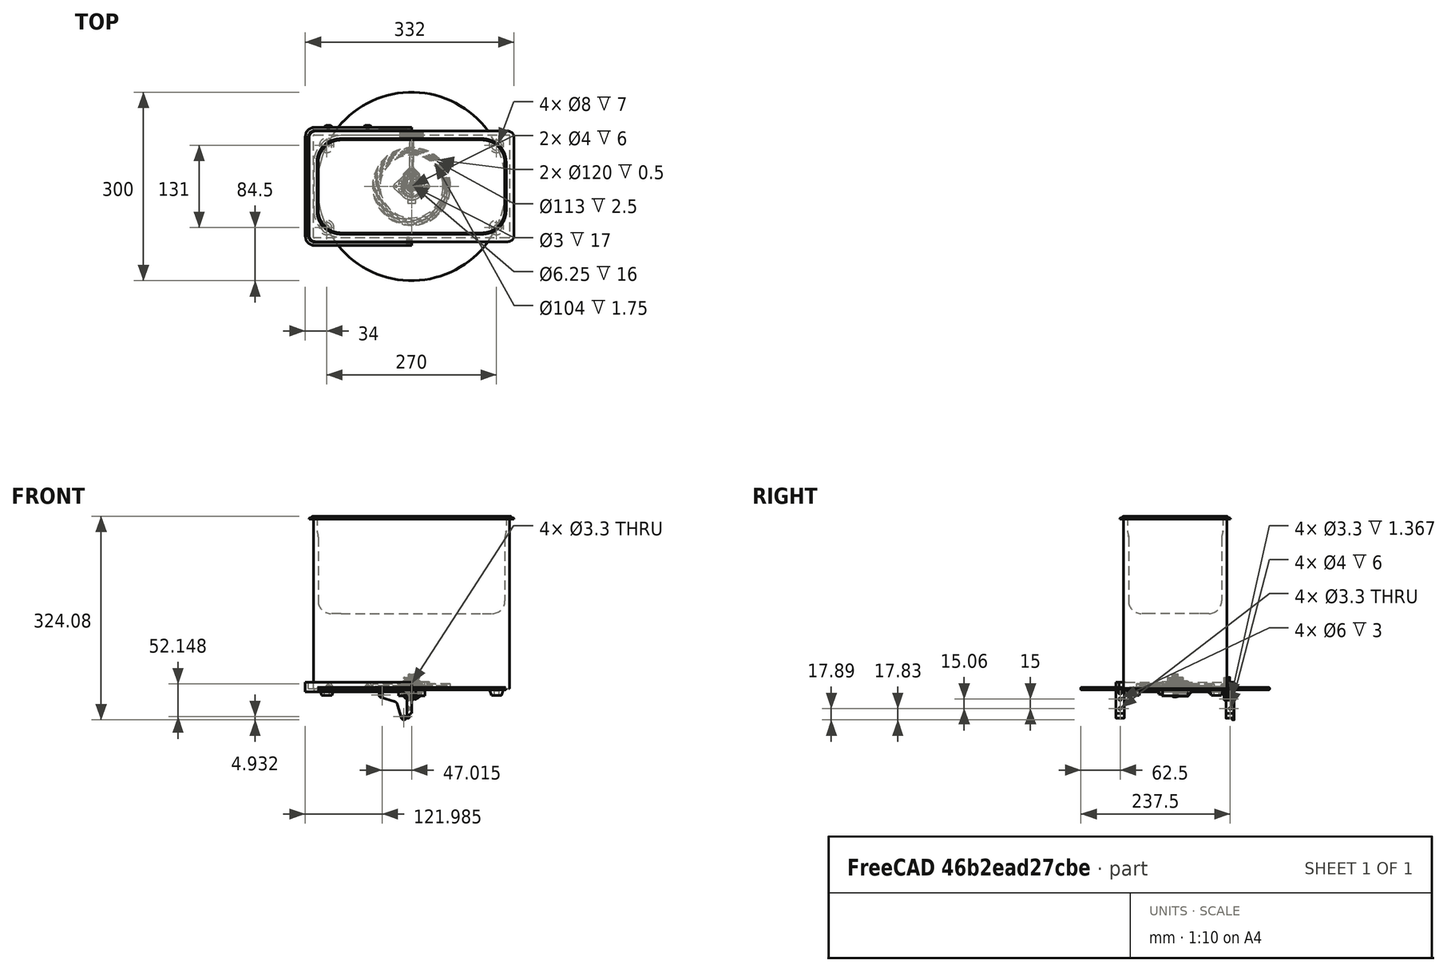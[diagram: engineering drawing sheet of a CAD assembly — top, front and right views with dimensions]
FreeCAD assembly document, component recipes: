
FREECAD ASSEMBLY — COMPONENT RECIPES ("assembly-ultrasonic-cleaner-exploded")

This assembly document has 14 components, labeled P0..P13 below (a component is one placed body or linked part). 14 of them carry a construction recipe — the FreeCAD feature program that regenerates the part from scratch, quoted from this document or its linked companion documents; the rest are supplied as boundary geometry only. No exploded tour is included for this assembly.
NOTE — document 2 of 2 of this assembly tour. The two overview renders and the header above are repeated from document 1; the component sections below continue where the previous document stopped.
COMPONENT P11 — recipe-attached ("Body011", modeled in this document).
Construction recipe (the document's own serialized feature program — sketch geometry with constraints, then the solid features built on it; lengths are millimeters unless a unit is written):

FEATURE [Sketcher::SketchObject] Sketch055
  ArcFitTolerance = 0
  AttachmentSupport = -> [XY_Plane011]
  ExternalBSplineMaxDegree = 0
  ExternalBSplineTolerance = 0
  FullyConstrained = false
  InternalTolerance = 1e-06
  InvalidShape = false
  MakeInternals = false
  MapMode = 5
  Support = -> [XY_Plane011]
  TreeRank = 0
  ValidateShape = false
  sketch-geometry (1):
    g0: Circle CenterX=0 CenterY=0 CenterZ=0 NormalX=0 NormalY=0 NormalZ=1 AngleXU=0 Radius=15
  constraints (2):
    c: Coincident(g0,g-1)
    c: Diameter(g0) = 30
FEATURE [PartDesign::Pad] Pad027
  AddSubType = 0
  AutoTaperInnerAngle = true
  CheckUpToFaceLimits = true
  ClaimChildren = false
  Direction = (1,1,1)
  Fit = 0
  FitJoin = 0
  InnerFit = 0
  InnerFitJoin = 0
  InvalidShape = false
  Length = 9
  Length2 = 100
  NewSolid = false
  Profile = -> Sketch055
  Suppress = false
  TaperInnerAngle = 0
  TaperInnerAngleRev = 0
  TreeRank = 0
  Type = 0
  ValidateShape = true
  _ProfileBasedVersion = 0
FEATURE [Sketcher::SketchObject] Sketch056
  ArcFitTolerance = 0
  AttachmentSupport = -> [Pad027]
  ExternalBSplineMaxDegree = 0
  ExternalBSplineTolerance = 0
  FullyConstrained = false
  InternalTolerance = 1e-06
  InvalidShape = false
  MakeInternals = false
  MapMode = 5
  Placement = pos=(0,0,9) rot=(0,0,1;0rad)
  Support = -> [Pad027]
  TreeRank = 0
  ValidateShape = false
  sketch-geometry (1):
    g0: Circle CenterX=0 CenterY=0 CenterZ=0 NormalX=0 NormalY=0 NormalZ=1 AngleXU=0 Radius=2
  constraints (2):
    c: Coincident(g0,g-1)
    c: Diameter(g0) = 4
FEATURE [PartDesign::Pocket] Pocket028
  AddSubType = 1
  AutoTaperInnerAngle = true
  BaseFeature = -> Pad027
  CheckUpToFaceLimits = true
  ClaimChildren = false
  Direction = (1,1,1)
  Fit = 0
  FitJoin = 0
  InnerFit = 0
  InnerFitJoin = 0
  InvalidShape = false
  Length = 8
  Length2 = 100
  NewSolid = false
  Profile = -> Sketch056
  Suppress = false
  TaperInnerAngle = 0
  TaperInnerAngleRev = 0
  TreeRank = 0
  Type = 0
  ValidateShape = true
  _ProfileBasedVersion = 0
  _Version = 0
FEATURE [Part::Part2DObjectPython] InvoluteGear001  # Draft 2D object (typed FeaturePython)
  AddendumCoefficient = 1
  AttachmentSupport = -> [Pocket028]
  DedendumCoefficient = 1.25
  ExternalGear = true
  HighPrecision = true
  InvalidShape = false
  MapMode = 5
  Modules = 0.55
  NumberOfTeeth = 17
  Placement = pos=(0,0,9) rot=(0,0,1;0rad)
  PressureAngle = 35
  ProfileShiftCoefficient = 0
  RootFilletCoefficient = 0.375
  Support = -> [Pocket028]
  TreeRank = 0
  ValidateShape = false
FEATURE [PartDesign::Pocket] Pocket029
  AddSubType = 1
  AutoTaperInnerAngle = true
  BaseFeature = -> Pocket028
  CheckUpToFaceLimits = true
  ClaimChildren = false
  Direction = (1,1,1)
  Fit = 0
  FitJoin = 0
  InnerFit = 0
  InnerFitJoin = 0
  InvalidShape = false
  Length = 0
  Length2 = 100
  NewSolid = false
  Profile = -> InvoluteGear001
  Suppress = false
  TaperInnerAngle = 0
  TaperInnerAngleRev = 0
  TreeRank = 0
  Type = 3
  UpToFace = -> Pocket028 [Face5]
  ValidateShape = true
  _ProfileBasedVersion = 0
  _Version = 0
FEATURE [Part::Part2DObjectPython] InvoluteGear002  # Draft 2D object (typed FeaturePython)
  AddendumCoefficient = 1
  DedendumCoefficient = 1.25
  ExternalGear = true
  HighPrecision = true
  InvalidShape = false
  Modules = 1.3
  NumberOfTeeth = 26
  PressureAngle = 20
  ProfileShiftCoefficient = 0
  RootFilletCoefficient = 0.375
  TreeRank = 0
  ValidateShape = false
FEATURE [PartDesign::Pad] Pad030
  AddSubType = 0
  AutoTaperInnerAngle = true
  BaseFeature = -> Pocket029
  CheckUpToFaceLimits = true
  ClaimChildren = false
  Direction = (1,1,1)
  Fit = 0
  FitJoin = 0
  InnerFit = 0
  InnerFitJoin = 0
  InvalidShape = false
  Length = 0.5
  Length2 = 100
  NewSolid = false
  Profile = -> InvoluteGear002
  Suppress = false
  TaperInnerAngle = 0
  TaperInnerAngleRev = 0
  TreeRank = 0
  Type = 0
  ValidateShape = true
  _ProfileBasedVersion = 0
FEATURE [PartDesign::Pad] Pad031
  AddSubType = 0
  AutoTaperInnerAngle = true
  BaseFeature = -> Pad030
  CheckUpToFaceLimits = true
  ClaimChildren = false
  Direction = (1,1,1)
  Fit = 0
  FitJoin = 0
  InnerFit = 0
  InnerFitJoin = 0
  InvalidShape = false
  Length = 8.5
  Length2 = 100
  NewSolid = false
  Profile = -> Pad030 [Face263]
  Suppress = false
  TaperInnerAngle = 0
  TaperInnerAngleRev = 0
  TreeRank = 0
  Type = 0
  ValidateShape = true
  _ProfileBasedVersion = 0
FEATURE [Sketcher::SketchObject] Sketch066
  ArcFitTolerance = 0
  AttachmentSupport = -> [YZ_Plane011]
  ExternalBSplineMaxDegree = 0
  ExternalBSplineTolerance = 0
  FullyConstrained = false
  InternalTolerance = 1e-06
  InvalidShape = false
  MakeInternals = false
  MapMode = 5
  Placement = pos=(0,0,0) rot=(0.57735,0.57735,0.57735;2.0944rad)
  Support = -> [YZ_Plane011]
  TreeRank = 0
  ValidateShape = false
  sketch-geometry (1):
    g0: Circle CenterX=0 CenterY=4.5 CenterZ=0 NormalX=0 NormalY=0 NormalZ=1 AngleXU=0 Radius=1.4
  constraints (3):
    c: PointOnObject(g0,g-2)
    c: DistanceY(g-1,g0) = 4.5
    c: Diameter(g0) = 2.8
FEATURE [PartDesign::Pocket] Pocket036
  AddSubType = 1
  AutoTaperInnerAngle = true
  BaseFeature = -> Pad031
  CheckUpToFaceLimits = true
  ClaimChildren = false
  Direction = (1,1,1)
  Fit = 0
  FitJoin = 0
  InnerFit = 0
  InnerFitJoin = 0
  InvalidShape = false
  Length = 5
  Length2 = 100
  NewSolid = false
  Profile = -> Sketch066
  Suppress = false
  TaperInnerAngle = 0
  TaperInnerAngleRev = 0
  TreeRank = 0
  Type = 1
  ValidateShape = true
  _ProfileBasedVersion = 0
  _Version = 0
FEATURE [Sketcher::SketchObject] Sketch067
  ArcFitTolerance = 0
  ExternalBSplineMaxDegree = 0
  ExternalBSplineTolerance = 0
  FullyConstrained = false
  InternalTolerance = 1e-06
  InvalidShape = false
  MakeInternals = false
  MapMode = 5
  Placement = pos=(-11,0,0) rot=(0.57735,0.57735,0.57735;2.0944rad)
  TreeRank = 0
  ValidateShape = false
  sketch-geometry (1):
    g0: Circle CenterX=0 CenterY=4.5 CenterZ=0 NormalX=0 NormalY=0 NormalZ=1 AngleXU=0 Radius=3
  constraints (3):
    c: PointOnObject(g0,g-2)
    c: Diameter(g0) = 6
    c: DistanceY(g-1,g0) = 4.5
FEATURE [PartDesign::Pocket] Pocket037
  AddSubType = 1
  AutoTaperInnerAngle = true
  BaseFeature = -> Pocket036
  CheckUpToFaceLimits = true
  ClaimChildren = false
  Direction = (1,1,1)
  Fit = 0
  FitJoin = 0
  InnerFit = 0
  InnerFitJoin = 0
  InvalidShape = false
  Length = 5
  Length2 = 100
  NewSolid = false
  Profile = -> Sketch067
  Suppress = false
  TaperInnerAngle = 0
  TaperInnerAngleRev = 0
  TreeRank = 0
  Type = 1
  ValidateShape = true
  _ProfileBasedVersion = 0
  _Version = 0
FEATURE [PartDesign::Chamfer] Chamfer021
  AddSubType = 0
  Angle = 45
  Base = -> Pocket037 [Edge1462]
  BaseFeature = -> Pocket037
  ChamferType = 1
  FlipDirection = false
  InvalidShape = false
  NewSolid = false
  Size = 0.25
  Size2 = 2
  SupportTransform = true
  Suppress = false
  TreeRank = 0
  UseAllEdges = false
  ValidateShape = true
FEATURE [PartDesign::Pad] Pad032
  AddSubType = 0
  AutoTaperInnerAngle = true
  BaseFeature = -> Chamfer021
  CheckUpToFaceLimits = true
  ClaimChildren = false
  Direction = (1,1,1)
  Fit = 0
  FitJoin = 0
  InnerFit = 0
  InnerFitJoin = 0
  InvalidShape = false
  Length = 5
  Length2 = 100
  NewSolid = false
  Profile = -> InvoluteGear002
  Reversed = true
  Suppress = false
  TaperInnerAngle = 0
  TaperInnerAngleRev = 0
  TreeRank = 0
  Type = 0
  ValidateShape = true
  _ProfileBasedVersion = 0
FEATURE [PartDesign::Fillet] Fillet016
  AddSubType = 0
  Base = -> Pad032 [Face439]
  BaseFeature = -> Pad032
  InvalidShape = false
  NewSolid = false
  Radius = 0.7
  SupportTransform = true
  Suppress = false
  TreeRank = 0
  UseAllEdges = false
  ValidateShape = true
FEATURE [Sketcher::SketchObject] Sketch083
  ArcFitTolerance = 0
  AttachmentSupport = -> [Fillet016]
  ExternalBSplineMaxDegree = 0
  ExternalBSplineTolerance = 0
  FullyConstrained = false
  InternalTolerance = 1e-06
  InvalidShape = false
  MakeInternals = false
  MapMode = 5
  Placement = pos=(0,0,9) rot=(0,0,1;0rad)
  Support = -> [Fillet016]
  TreeRank = 0
  ValidateShape = false
  sketch-geometry (2):
    g0: Circle CenterX=0 CenterY=0 CenterZ=0 NormalX=0 NormalY=0 NormalZ=1 AngleXU=0 Radius=6.75
    g1: Circle CenterX=0 CenterY=0 CenterZ=0 NormalX=0 NormalY=0 NormalZ=1 AngleXU=0 Radius=20
  constraints (4):
    c: Coincident(g0,g-1)
    c: Diameter(g0) = 13.5
    c: Coincident(g1,g0)
    c: Diameter(g1) = 40
FEATURE [PartDesign::Pocket] Pocket046
  AddSubType = 1
  AutoTaperInnerAngle = true
  BaseFeature = -> Fillet016
  CheckUpToFaceLimits = true
  ClaimChildren = false
  Direction = (1,1,1)
  Fit = 0
  FitJoin = 0
  InnerFit = 0
  InnerFitJoin = 0
  InvalidShape = false
  Length = 2
  Length2 = 100
  NewSolid = false
  Profile = -> Sketch083
  Suppress = false
  TaperInnerAngle = 0
  TaperInnerAngleRev = 0
  TreeRank = 0
  Type = 0
  ValidateShape = true
  _ProfileBasedVersion = 0
  _Version = 0
FEATURE [PartDesign::Chamfer] Chamfer031
  AddSubType = 0
  Angle = 45
  Base = -> Pocket046 [Edge1096]
  BaseFeature = -> Pocket046
  ChamferType = 0
  FlipDirection = false
  InvalidShape = false
  NewSolid = false
  Size = 1.9
  Size2 = 1
  SupportTransform = true
  Suppress = false
  TreeRank = 0
  UseAllEdges = false
  ValidateShape = true
FEATURE [PartDesign::Body] Body011
  AutoGroupSolids = false
  ClaimAllChildren = false
  ExportMode = 0
  Group = -> [Sketch055,Pad027,Sketch056,Pocket028,InvoluteGear001,Pocket029,InvoluteGear002,Pad030,Pad031,Sketch066,Pocket036,Sketch067,Pocket037,Chamfer021,Pad032,Fillet016,Sketch083,Pocket046,Chamfer031]
  InvalidShape = false
  Origin = -> Origin011
  SingleSolid = true
  Tip = -> Chamfer031
  TreeRank = 0
  ValidateShape = false
  _ExportChildren = -> [Pad027,Pocket028,Pocket029,Pad030,Pad031,Pocket036,Pocket037,Chamfer021,Pad032,Fillet016,Pocket046,Chamfer031]
  _GroupVersion = 1
COMPONENT P12 — recipe-attached ("Body012", modeled in this document).
Construction recipe (the document's own serialized feature program — sketch geometry with constraints, then the solid features built on it; lengths are millimeters unless a unit is written):

FEATURE [Sketcher::SketchObject] Sketch068
  ArcFitTolerance = 0
  ExternalBSplineMaxDegree = 0
  ExternalBSplineTolerance = 0
  FullyConstrained = false
  InternalTolerance = 1e-06
  InvalidShape = false
  MakeInternals = false
  MapMode = 5
  Placement = pos=(0,0,1.75) rot=(1,0,0;3.14159rad)
  TreeRank = 0
  ValidateShape = false
  sketch-geometry (2):
    g0: Circle CenterX=0 CenterY=0 CenterZ=0 NormalX=0 NormalY=0 NormalZ=1 AngleXU=0 Radius=53.5
    g1: Circle CenterX=0 CenterY=0 CenterZ=0 NormalX=0 NormalY=0 NormalZ=1 AngleXU=0 Radius=56.5
  constraints (4):
    c: Coincident(g0,g-1)
    c: Coincident(g1,g0)
    c: Diameter(g0) = 107
    c: Diameter(g1) = 113
FEATURE [PartDesign::ShapeBinder] CopyMirrored003
  InvalidShape = false
  TraceSupport = false
  TreeRank = 0
  ValidateShape = false
FEATURE [Sketcher::SketchObject] Sketch070
  ArcFitTolerance = 0
  AttachmentSupport = -> [CopyMirrored003]
  ExternalBSplineMaxDegree = 0
  ExternalBSplineTolerance = 0
  FullyConstrained = false
  InternalTolerance = 1e-06
  InvalidShape = false
  MakeInternals = false
  MapMode = 5
  Placement = pos=(0,0,1.75) rot=(0,0,1;0rad)
  Support = -> [CopyMirrored003]
  TreeRank = 0
  ValidateShape = false
  sketch-geometry (2):
    g0: Circle CenterX=0 CenterY=0 CenterZ=0 NormalX=0 NormalY=0 NormalZ=1 AngleXU=0 Radius=62
    g1: Circle [constr] CenterX=0 CenterY=0 CenterZ=0 NormalX=0 NormalY=0 NormalZ=1 AngleXU=0 Radius=52
  constraints (4):
    c: Coincident(g0,g-1)
    c: Radius(g0) = 62
    c: Coincident(g1,g0)
    c: Radius(g1) = 52
FEATURE [Sketcher::SketchObject] Sketch071
  ArcFitTolerance = 0
  ExternalBSplineMaxDegree = 0
  ExternalBSplineTolerance = 0
  FullyConstrained = false
  InternalTolerance = 1e-06
  InvalidShape = false
  MakeInternals = false
  MapMode = 5
  Placement = pos=(0,0,-8.25) rot=(1,0,0;3.14159rad)
  TreeRank = 0
  ValidateShape = false
  sketch-geometry (1):
    g0: Circle CenterX=0 CenterY=0 CenterZ=0 NormalX=0 NormalY=0 NormalZ=1 AngleXU=0 Radius=1.5
  constraints (2):
    c: Coincident(g0,g-1)
    c: Diameter(g0) = 3
FEATURE [PartDesign::Pad] Pad034
  AddSubType = 0
  AllowMultiFace = false
  AutoTaperInnerAngle = true
  CheckUpToFaceLimits = true
  ClaimChildren = false
  Direction = (1,1,1)
  Fit = 0
  FitJoin = 0
  InnerFit = 0
  InnerFitJoin = 0
  InvalidShape = false
  Length = 6
  Length2 = 100
  NewSolid = false
  Profile = -> Sketch070
  Suppress = false
  TaperInnerAngle = 0
  TaperInnerAngleRev = 0
  TreeRank = 0
  Type = 0
  ValidateShape = true
  _ProfileBasedVersion = 0
FEATURE [Sketcher::SketchObject] Sketch074
  ArcFitTolerance = 0
  AttachmentSupport = -> [Pad034]
  ExternalBSplineMaxDegree = 0
  ExternalBSplineTolerance = 0
  FullyConstrained = false
  InternalTolerance = 1e-06
  InvalidShape = false
  MakeInternals = false
  MapMode = 5
  Placement = pos=(0,0,1.75) rot=(1,0,0;3.14159rad)
  Support = -> [Pad034]
  TreeRank = 0
  ValidateShape = false
  sketch-geometry (1):
    g0: Circle CenterX=0 CenterY=0 CenterZ=0 NormalX=0 NormalY=0 NormalZ=1 AngleXU=0 Radius=3
  constraints (2):
    c: Coincident(g0,g-1)
    c: Diameter(g0) = 6
FEATURE [PartDesign::Pad] Pad033
  AddSubType = 0
  AllowMultiFace = false
  AutoTaperInnerAngle = true
  BaseFeature = -> Pad034
  CheckUpToFaceLimits = true
  ClaimChildren = false
  Direction = (1,1,1)
  Fit = 0
  FitJoin = 0
  InnerFit = 0
  InnerFitJoin = 0
  InvalidShape = false
  Length = 15
  Length2 = 100
  NewSolid = false
  Profile = -> Sketch074
  Suppress = false
  TaperInnerAngle = 0
  TaperInnerAngleRev = 0
  TreeRank = 0
  Type = 0
  ValidateShape = true
  _ProfileBasedVersion = 0
FEATURE [PartDesign::Pocket] Pocket040
  AddSubType = 1
  AllowMultiFace = false
  AutoTaperInnerAngle = true
  BaseFeature = -> Pad033
  CheckUpToFaceLimits = true
  ClaimChildren = false
  Direction = (1,1,1)
  Fit = 0
  FitJoin = 0
  InnerFit = 0
  InnerFitJoin = 0
  InvalidShape = false
  Length = 5
  Length2 = 100
  Midplane = true
  NewSolid = false
  Profile = -> Sketch071
  Reversed = true
  Suppress = false
  TaperInnerAngle = 0
  TaperInnerAngleRev = 0
  TreeRank = 0
  Type = 1
  ValidateShape = true
  _ProfileBasedVersion = 0
  _Version = 0
FEATURE [PartDesign::Pocket] Pocket041
  AddSubType = 1
  AllowMultiFace = false
  AutoTaperInnerAngle = true
  BaseFeature = -> Pocket040
  CheckUpToFaceLimits = true
  ClaimChildren = false
  Direction = (1,1,1)
  Fit = 0
  FitJoin = 0
  InnerFit = 0
  InnerFitJoin = 0
  InvalidShape = false
  Length = 3
  Length2 = 100
  NewSolid = false
  Profile = -> Sketch068
  Suppress = false
  TaperInnerAngle = 0
  TaperInnerAngleRev = 0
  TreeRank = 0
  Type = 0
  ValidateShape = true
  _ProfileBasedVersion = 0
  _Version = 0
FEATURE [PartDesign::Draft] Draft007
  AddSubType = 0
  Angle = 5
  Base = -> Pocket041 [Face8]
  BaseFeature = -> Pocket041
  InvalidShape = false
  NeutralPlane = -> Pocket041 [Face3]
  NewSolid = false
  SupportTransform = false
  Suppress = false
  TreeRank = 0
  ValidateShape = true
FEATURE [PartDesign::Draft] Draft008
  AddSubType = 0
  Angle = 5
  Base = -> Draft007 [Face4]
  BaseFeature = -> Draft007
  InvalidShape = false
  NeutralPlane = -> Draft007 [Face10]
  NewSolid = false
  SupportTransform = false
  Suppress = false
  TreeRank = 0
  ValidateShape = true
FEATURE [Sketcher::SketchObject] Sketch075
  ArcFitTolerance = 0
  AttachmentSupport = -> [Draft008]
  ExternalBSplineMaxDegree = 0
  ExternalBSplineTolerance = 0
  ExternalGeometry = -> [Draft008]
  FullyConstrained = false
  InternalTolerance = 1e-06
  InvalidShape = false
  MakeInternals = false
  MapMode = 5
  Placement = pos=(0,0,7.75) rot=(0,0,1;0rad)
  Support = -> [Draft008]
  TreeRank = 0
  ValidateShape = false
  sketch-geometry (2):
    g0: Circle CenterX=0 CenterY=0 CenterZ=0 NormalX=0 NormalY=0 NormalZ=1 AngleXU=0 Radius=1.5
    g1: Circle CenterX=0 CenterY=0 CenterZ=0 NormalX=0 NormalY=0 NormalZ=1 AngleXU=0 Radius=12.5
  constraints (3):
    c: Coincident(g0,g-1)
    c: Coincident(g1,g0)
    c: Diameter(g1) = 25
FEATURE [PartDesign::Pad] Pad035
  AddSubType = 0
  AutoTaperInnerAngle = true
  BaseFeature = -> Draft008
  CheckUpToFaceLimits = true
  ClaimChildren = false
  Direction = (1,1,1)
  Fit = 0
  FitJoin = 0
  InnerFit = 0
  InnerFitJoin = 0
  InvalidShape = false
  Length = 5
  Length2 = 100
  NewSolid = false
  Profile = -> Sketch075
  Suppress = false
  TaperInnerAngle = 0
  TaperInnerAngleRev = 0
  TreeRank = 0
  Type = 0
  ValidateShape = true
  _ProfileBasedVersion = 0
FEATURE [Sketcher::SketchObject] Sketch072
  ArcFitTolerance = 0
  AttachmentSupport = -> [Pad035]
  ExternalBSplineMaxDegree = 0
  ExternalBSplineTolerance = 0
  FullyConstrained = false
  InternalTolerance = 1e-06
  InvalidShape = false
  MakeInternals = false
  MapMode = 5
  Placement = pos=(0,0,12.75) rot=(0,0,1;0rad)
  Support = -> [Pad035]
  TreeRank = 0
  ValidateShape = false
  sketch-geometry (1):
    g0: Circle CenterX=0 CenterY=0 CenterZ=0 NormalX=0 NormalY=0 NormalZ=1 AngleXU=0 Radius=2
  constraints (2):
    c: Coincident(g0,g-1)
    c: Diameter(g0) = 4
FEATURE [PartDesign::Pocket] Pocket042
  AddSubType = 1
  AutoTaperInnerAngle = true
  BaseFeature = -> Pad035
  CheckUpToFaceLimits = true
  ClaimChildren = false
  Direction = (1,1,1)
  Fit = 0
  FitJoin = 0
  InnerFit = 0
  InnerFitJoin = 0
  InvalidShape = false
  Length = 9
  Length2 = 100
  NewSolid = false
  Profile = -> Sketch072
  Suppress = false
  TaperInnerAngle = 0
  TaperInnerAngleRev = 0
  TreeRank = 0
  Type = 0
  ValidateShape = true
  _ProfileBasedVersion = 0
  _Version = 0
FEATURE [Sketcher::SketchObject] Sketch073
  ArcFitTolerance = 0
  AttachmentSupport = -> [Pocket042]
  ExternalBSplineMaxDegree = 0
  ExternalBSplineTolerance = 0
  FullyConstrained = false
  InternalTolerance = 1e-06
  InvalidShape = false
  MakeInternals = false
  MapMode = 5
  Placement = pos=(0,0,12.75) rot=(0,0,1;0rad)
  Support = -> [Pocket042]
  TreeRank = 0
  ValidateShape = false
  sketch-geometry (1):
    g0: Circle CenterX=0 CenterY=0 CenterZ=0 NormalX=0 NormalY=0 NormalZ=1 AngleXU=0 Radius=3
  constraints (2):
    c: Coincident(g0,g-1)
    c: Diameter(g0) = 6
FEATURE [PartDesign::Pocket] Pocket039
  AddSubType = 1
  AutoTaperInnerAngle = true
  BaseFeature = -> Pocket042
  CheckUpToFaceLimits = true
  ClaimChildren = false
  Direction = (1,1,1)
  Fit = 0
  FitJoin = 0
  InnerFit = 0
  InnerFitJoin = 0
  InvalidShape = false
  Length = 3
  Length2 = 100
  NewSolid = false
  Profile = -> Sketch073
  Suppress = false
  TaperInnerAngle = 0
  TaperInnerAngleRev = 0
  TreeRank = 0
  Type = 0
  ValidateShape = true
  _ProfileBasedVersion = 0
  _Version = 0
FEATURE [PartDesign::Fillet] Fillet017
  AddSubType = 0
  Base = -> Pocket039 [Edge5]
  BaseFeature = -> Pocket039
  InvalidShape = false
  NewSolid = false
  Radius = 4
  SupportTransform = true
  Suppress = false
  TreeRank = 0
  UseAllEdges = false
  ValidateShape = true
FEATURE [PartDesign::Chamfer] Chamfer025
  AddSubType = 0
  Angle = 45
  Base = -> Fillet017 [Face6]
  BaseFeature = -> Fillet017
  ChamferType = 0
  FlipDirection = false
  InvalidShape = false
  NewSolid = false
  Size = 0.5
  Size2 = 1
  SupportTransform = true
  Suppress = false
  TreeRank = 0
  UseAllEdges = false
  ValidateShape = true
FEATURE [PartDesign::Chamfer] Chamfer022
  AddSubType = 0
  Angle = 45
  Base = -> Chamfer025 [Face7]
  BaseFeature = -> Chamfer025
  ChamferType = 0
  FlipDirection = false
  InvalidShape = false
  NewSolid = false
  Size = 1
  Size2 = 1
  SupportTransform = true
  Suppress = false
  TreeRank = 0
  UseAllEdges = false
  ValidateShape = true
FEATURE [PartDesign::Chamfer] Chamfer024
  AddSubType = 0
  Angle = 45
  Base = -> Chamfer022 [Edge31]
  BaseFeature = -> Chamfer022
  ChamferType = 0
  FlipDirection = false
  InvalidShape = false
  NewSolid = false
  Size = 0.5
  Size2 = 1
  SupportTransform = true
  Suppress = false
  TreeRank = 0
  UseAllEdges = false
  ValidateShape = true
FEATURE [Sketcher::SketchObject] Sketch069
  ArcFitTolerance = 0
  AttachmentSupport = -> [Chamfer024]
  ExternalBSplineMaxDegree = 0
  ExternalBSplineTolerance = 0
  FullyConstrained = false
  InternalTolerance = 1e-06
  InvalidShape = false
  MakeInternals = false
  MapMode = 5
  Placement = pos=(0,0,12.75) rot=(0,0,1;0rad)
  Support = -> [Chamfer024]
  TreeRank = 0
  ValidateShape = false
  sketch-geometry (2):
    g0: Circle CenterX=0 CenterY=7.5 CenterZ=0 NormalX=0 NormalY=0 NormalZ=1 AngleXU=0 Radius=2
    g1: Circle CenterX=0 CenterY=-7.5 CenterZ=0 NormalX=0 NormalY=0 NormalZ=1 AngleXU=0 Radius=2
  constraints (5):
    c: PointOnObject(g0,g-2)
    c: Symmetric(g1,g0,g-1)
    c: Equal(g0,g1)
    c: DistanceY(g-1,g0) = 7.5
    c: Diameter(g0) = 4
FEATURE [PartDesign::Pocket] Pocket038
  AddSubType = 1
  AutoTaperInnerAngle = true
  BaseFeature = -> Chamfer024
  CheckUpToFaceLimits = true
  ClaimChildren = false
  Direction = (1,1,1)
  Fit = 0
  FitJoin = 0
  InnerFit = 0
  InnerFitJoin = 0
  InvalidShape = false
  Length = 6
  Length2 = 100
  NewSolid = false
  Profile = -> Sketch069
  Suppress = false
  TaperInnerAngle = 0
  TaperInnerAngleRev = 0
  TreeRank = 0
  Type = 0
  ValidateShape = true
  _ProfileBasedVersion = 0
  _Version = 0
FEATURE [PartDesign::Chamfer] Chamfer023
  AddSubType = 0
  Angle = 45
  Base = -> Pocket038 [Edge32,Edge31]
  BaseFeature = -> Pocket038
  ChamferType = 0
  FlipDirection = false
  InvalidShape = false
  NewSolid = false
  Size = 0.5
  Size2 = 1
  SupportTransform = true
  Suppress = false
  TreeRank = 0
  UseAllEdges = false
  ValidateShape = true
FEATURE [PartDesign::Body] Body012
  AutoGroupSolids = false
  ClaimAllChildren = false
  ExportMode = 0
  Group = -> [CopyMirrored003,Sketch070,Pad034,Sketch074,Pad033,Sketch071,Pocket040,Sketch068,Pocket041,Draft007,Draft008,Sketch075,Pad035,Sketch072,Pocket042,Sketch073,Pocket039,Fillet017,Chamfer025,Chamfer022,Chamfer024,Sketch069,Pocket038,Chamfer023]
  InvalidShape = false
  Origin = -> Origin012
  SingleSolid = true
  Tip = -> Chamfer023
  TreeRank = 0
  ValidateShape = false
  _ExportChildren = -> [CopyMirrored003,Pad034,Pad033,Pocket040,Pocket041,Draft007,Draft008,Pad035,Pocket042,Pocket039,Fillet017,Chamfer025,Chamfer022,Chamfer024,Pocket038,Chamfer023]
  _GroupVersion = 1
COMPONENT P13 — recipe-attached ("Body013", modeled in this document).
Construction recipe (the document's own serialized feature program — sketch geometry with constraints, then the solid features built on it; lengths are millimeters unless a unit is written):

FEATURE [Sketcher::SketchObject] Sketch076
  ArcFitTolerance = 0
  AttachmentSupport = -> [XY_Plane013]
  ExternalBSplineMaxDegree = 0
  ExternalBSplineTolerance = 0
  FullyConstrained = false
  InternalTolerance = 1e-06
  InvalidShape = false
  MakeInternals = false
  MapMode = 5
  Support = -> [XY_Plane013]
  TreeRank = 0
  ValidateShape = false
  sketch-geometry (7):
    g0: LineSegment StartX=0 StartY=0 StartZ=0 EndX=12.5 EndY=0 EndZ=0
    g1: LineSegment StartX=12.5 StartY=0 StartZ=0 EndX=12.5 EndY=20 EndZ=0
    g2: LineSegment StartX=12.5 StartY=20 StartZ=0 EndX=3 EndY=30 EndZ=0
    g3: LineSegment StartX=3 StartY=30 StartZ=0 EndX=3 EndY=82 EndZ=0
    g4: LineSegment StartX=3 StartY=82 StartZ=0 EndX=0 EndY=82 EndZ=0
    g5: LineSegment StartX=0 StartY=82 StartZ=0 EndX=0 EndY=0 EndZ=0
    g6: LineSegment [constr] StartX=0 StartY=0 StartZ=0 EndX=-12.5 EndY=1e-16 EndZ=0
  constraints (19):
    c: Coincident(g-1,g0)
    c: PointOnObject(g0,g-1)
    c: Coincident(g0,g1)
    c: Vertical(g1)
    c: Coincident(g1,g2)
    c: Coincident(g2,g3)
    c: Vertical(g3)
    c: Coincident(g3,g4)
    c: Horizontal(g4)
    c: Coincident(g4,g5)
    c: Coincident(g5,g0)
    c: Vertical(g5)
    c: DistanceX(g4,g4) = 3
    c: Coincident(g6,g0)
    c: Symmetric(g6,g0,g-2)
    c: DistanceX(g6,g0) = 25
    c: DistanceY(g1,g2) = 10
    c: DistanceY(g5,g5) = 82
    c: DistanceY(g1,g1) = 20
FEATURE [PartDesign::Revolution] Revolution004
  AddSubType = 0
  Angle = 360
  Axis = (0,1,0)
  Base = (0,0,0)
  ClaimChildren = false
  Fit = 0
  FitJoin = 0
  InnerFit = 0
  InnerFitJoin = 0
  InvalidShape = false
  NewSolid = false
  Profile = -> Sketch076
  ReferenceAxis = -> Sketch076 [V_Axis]
  Reversed = true
  Suppress = false
  TreeRank = 0
  ValidateShape = true
  _ProfileBasedVersion = 0
FEATURE [Sketcher::SketchObject] Sketch077
  ArcFitTolerance = 0
  AttachmentSupport = -> [Revolution004]
  ExternalBSplineMaxDegree = 0
  ExternalBSplineTolerance = 0
  FullyConstrained = false
  InternalTolerance = 1e-06
  InvalidShape = false
  MakeInternals = false
  MapMode = 5
  Placement = pos=(0,0,0) rot=(1,0,0;1.5708rad)
  Support = -> [Revolution004]
  TreeRank = 0
  ValidateShape = false
  sketch-geometry (2):
    g0: Circle CenterX=0 CenterY=7.5 CenterZ=0 NormalX=0 NormalY=0 NormalZ=1 AngleXU=0 Radius=1.65
    g1: Circle CenterX=0 CenterY=-7.5 CenterZ=0 NormalX=0 NormalY=0 NormalZ=1 AngleXU=0 Radius=1.65
  constraints (5):
    c: PointOnObject(g0,g-2)
    c: Symmetric(g0,g1,g-1)
    c: Equal(g0,g1)
    c: DistanceY(g1,g0) = 15
    c: Diameter(g0) = 3.3
FEATURE [PartDesign::Pocket] Pocket044
  AddSubType = 1
  AutoTaperInnerAngle = true
  BaseFeature = -> Revolution004
  CheckUpToFaceLimits = true
  ClaimChildren = false
  Direction = (1,1,1)
  Fit = 0
  FitJoin = 0
  InnerFit = 0
  InnerFitJoin = 0
  InvalidShape = false
  Length = 5
  Length2 = 100
  NewSolid = false
  Profile = -> Sketch077
  Suppress = false
  TaperInnerAngle = 0
  TaperInnerAngleRev = 0
  TreeRank = 0
  Type = 1
  ValidateShape = true
  _ProfileBasedVersion = 0
  _Version = 0
FEATURE [Sketcher::SketchObject] Sketch078
  ArcFitTolerance = 0
  AttachmentSupport = -> [Plane009]
  ExternalBSplineMaxDegree = 0
  ExternalBSplineTolerance = 0
  ExternalGeometry = -> [Pocket044,Pocket]
  FullyConstrained = false
  InternalTolerance = 1e-06
  InvalidShape = false
  MakeInternals = false
  MapMode = 5
  Placement = pos=(0,4,0) rot=(-0.57735,-0.57735,-0.57735;2.0944rad)
  Support = -> [Plane009]
  TreeRank = 0
  ValidateShape = false
  sketch-geometry (8):
    g0: ArcOfCircle CenterX=7.5 CenterY=1.7e-15 CenterZ=0 NormalX=0 NormalY=0 NormalZ=1 AngleXU=0 Radius=3 StartAngle=1.98231 EndAngle=4.30087
    g1: ArcOfCircle CenterX=-7.5 CenterY=-1.7e-15 CenterZ=0 NormalX=0 NormalY=0 NormalZ=1 AngleXU=0 Radius=3 StartAngle=5.12391 EndAngle=7.44246
    g2: LineSegment StartX=6.3 StartY=2.74955 StartZ=0 EndX=11.4564 EndY=5 EndZ=0
    g3: LineSegment StartX=6.3 StartY=-2.74955 StartZ=0 EndX=11.4564 EndY=-5 EndZ=0
    g4: LineSegment StartX=-6.3 StartY=-2.74955 StartZ=0 EndX=-11.4564 EndY=-5 EndZ=0
    g5: LineSegment StartX=-6.3 StartY=2.74955 StartZ=0 EndX=-11.4564 EndY=5 EndZ=0
    g6: ArcOfCircle CenterX=0 CenterY=0 CenterZ=0 NormalX=0 NormalY=0 NormalZ=1 AngleXU=0 Radius=12.5 StartAngle=5.87167 EndAngle=6.6947
    g7: ArcOfCircle CenterX=0 CenterY=0 CenterZ=0 NormalX=0 NormalY=0 NormalZ=1 AngleXU=0 Radius=12.5 StartAngle=2.73008 EndAngle=3.55311
  constraints (12):
    c: Equal(g0,g1)
    c: Tangent(g4,g1) = 1.5708
    c: Tangent(g5,g1) = -1.5708
    c: Tangent(g2,g0) = 1.5708
    c: Tangent(g3,g0) = -1.5708
    c: Radius(g0) = 3
    c: Coincident(g6,g-1)
    c: Coincident(g6,g2)
    c: Coincident(g6,g3)
    c: Coincident(g7,g6)
    c: Coincident(g7,g4)
    c: Coincident(g7,g5)
FEATURE [PartDesign::Pocket] Pocket043
  AddSubType = 1
  AutoTaperInnerAngle = true
  BaseFeature = -> Pocket044
  CheckUpToFaceLimits = true
  ClaimChildren = false
  Direction = (1,1,1)
  Fit = 0
  FitJoin = 0
  InnerFit = 0
  InnerFitJoin = 0
  InvalidShape = false
  Length = 5
  Length2 = 100
  NewSolid = false
  Profile = -> Sketch078
  Reversed = true
  Suppress = false
  TaperInnerAngle = 0
  TaperInnerAngleRev = 0
  TreeRank = 0
  Type = 1
  ValidateShape = true
  _ProfileBasedVersion = 0
  _Version = 0
FEATURE [PartDesign::Chamfer] Chamfer026
  AddSubType = 0
  Angle = 45
  Base = -> Pocket043 [Face1,Edge15,Edge17]
  BaseFeature = -> Pocket043
  ChamferType = 0
  FlipDirection = false
  InvalidShape = false
  NewSolid = false
  Size = 0.5
  Size2 = 1
  SupportTransform = true
  Suppress = false
  TreeRank = 0
  UseAllEdges = false
  ValidateShape = true
FEATURE [PartDesign::Chamfer] Chamfer027
  AddSubType = 0
  Angle = 45
  Base = -> Chamfer026 [Edge14,Edge17]
  BaseFeature = -> Chamfer026
  ChamferType = 0
  FlipDirection = false
  InvalidShape = false
  NewSolid = false
  Size = 2.25
  Size2 = 1
  SupportTransform = true
  Suppress = false
  TreeRank = 0
  UseAllEdges = false
  ValidateShape = true
FEATURE [PartDesign::Fillet] Fillet018
  AddSubType = 0
  Base = -> Chamfer027 [Edge15,Edge4,Edge9,Edge29]
  BaseFeature = -> Chamfer027
  InvalidShape = false
  NewSolid = false
  Radius = 5
  SupportTransform = true
  Suppress = false
  TreeRank = 0
  UseAllEdges = false
  ValidateShape = true
FEATURE [PartDesign::Fillet] Fillet019
  AddSubType = 0
  Base = -> Fillet018 [Edge48,Edge44,Edge46]
  BaseFeature = -> Fillet018
  InvalidShape = false
  NewSolid = false
  Radius = 2
  SupportTransform = true
  Suppress = false
  TreeRank = 0
  UseAllEdges = false
  ValidateShape = true
FEATURE [PartDesign::Chamfer] Chamfer028
  AddSubType = 0
  Angle = 45
  Base = -> Fillet019 [Face50]
  BaseFeature = -> Fillet019
  ChamferType = 0
  FlipDirection = false
  InvalidShape = false
  NewSolid = false
  Size = 1
  Size2 = 1
  SupportTransform = true
  Suppress = false
  TreeRank = 0
  UseAllEdges = false
  ValidateShape = true
FEATURE [PartDesign::Body] Body013
  AutoGroupSolids = false
  ClaimAllChildren = false
  ExportMode = 0
  Group = -> [Sketch076,Revolution004,Sketch077,Pocket044,Sketch078,Pocket043,Chamfer026,Chamfer027,Fillet018,Fillet019,Chamfer028]
  InvalidShape = false
  Origin = -> Origin013
  SingleSolid = true
  Tip = -> Chamfer028
  TreeRank = 0
  ValidateShape = false
  _ExportChildren = -> [Revolution004,Pocket044,Pocket043,Chamfer026,Chamfer027,Fillet018,Fillet019,Chamfer028]
  _GroupVersion = 1
PROVENANCE & LICENSES
A FreeCAD (.FCStd) document from a public repository crawl; recipes are the document's own serialized feature recipes (and, for linked parts, companion documents' recipes).
License: as declared in the source repository (recorded in the dataset sidecar).
